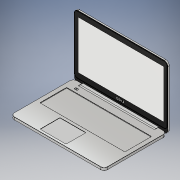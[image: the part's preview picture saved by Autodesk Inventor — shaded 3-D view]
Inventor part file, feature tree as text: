
AUTODESK INVENTOR PART (.ipt)
format: ipt  version: 2018 (Build 220112000, 112)  size: 2,366,464 bytes
history: native  units: in
note: dims shown in document units (in); Inventor stores cm internally (conversion verified against a paired STEP export)
features: imported_body x119, split x4, sketch x4, boolean_combine x3, projected_geometry x1
ambient origin geometry x8: Origin, YZ Plane, XZ Plane, XY Plane, X Axis, Y Axis, Z Axis, Center Point
bodies: Solid1 (feature_tree), Solid2 (feature_tree), Solid3 (feature_tree), Solid4 (feature_tree), Solid5 (feature_tree), Solid6 (feature_tree), Solid7 (feature_tree), Solid8 (feature_tree), Solid9 (feature_tree), Solid10 (feature_tree), Solid11 (feature_tree), Solid12 (feature_tree), Solid13 (feature_tree), Solid14 (feature_tree), Solid15 (feature_tree), Solid16 (feature_tree), Solid17 (feature_tree), Solid18 (feature_tree), Solid19 (feature_tree), Solid20 (feature_tree), Solid21 (feature_tree), Solid22 (feature_tree), Solid23 (feature_tree), Solid24 (feature_tree), Solid25 (feature_tree), Solid26 (feature_tree), Solid27 (feature_tree), Solid28 (feature_tree), Solid29 (feature_tree), Solid30 (feature_tree), Solid31 (feature_tree), Solid32 (feature_tree), Solid33 (feature_tree), Solid34 (feature_tree), Solid35 (feature_tree), Solid36 (feature_tree), Solid37 (feature_tree), Solid38 (feature_tree), Solid39 (feature_tree), Solid40 (feature_tree), Solid41 (feature_tree), Solid42 (feature_tree), Solid43 (feature_tree), Solid44 (feature_tree), Solid45 (feature_tree), Solid46 (feature_tree), Solid47 (feature_tree), Solid48 (feature_tree), Solid49 (feature_tree), Solid50 (feature_tree), Solid51 (feature_tree), Solid52 (feature_tree), Solid53 (feature_tree), Solid54 (feature_tree), Solid55 (feature_tree), Solid56 (feature_tree), Solid57 (feature_tree), Solid58 (feature_tree), Solid59 (feature_tree), Solid60 (feature_tree), Solid61 (feature_tree), Solid62 (feature_tree), Solid63 (feature_tree), Solid64 (feature_tree), Solid65 (feature_tree), Solid66 (feature_tree), Solid67 (feature_tree), Solid68 (feature_tree), Solid69 (feature_tree), Solid70 (feature_tree), Solid71 (feature_tree), Solid72 (feature_tree), Solid73 (feature_tree), Solid74 (feature_tree), Solid75 (feature_tree), Solid76 (feature_tree), Solid77 (feature_tree), Solid78 (feature_tree), Solid79 (feature_tree), Solid80 (feature_tree), Solid81 (feature_tree), Solid82 (feature_tree), Solid83 (feature_tree), Solid84 (feature_tree), Solid85 (feature_tree), Solid86 (feature_tree), Solid87 (feature_tree), Solid88 (feature_tree), Solid89 (feature_tree), Solid90 (feature_tree), Solid91 (feature_tree), Solid92 (feature_tree), Solid93 (feature_tree), Solid94 (feature_tree), Solid95 (feature_tree), Solid96 (feature_tree), Solid97 (feature_tree), Solid98 (feature_tree), Solid99 (feature_tree), Solid100 (feature_tree), Solid101 (feature_tree), Solid102 (feature_tree), Solid103 (feature_tree), Solid104 (feature_tree), Solid105 (feature_tree), Solid106 (feature_tree), Solid107 (feature_tree), Solid108 (feature_tree), Solid109 (feature_tree), Solid110 (feature_tree), Solid111 (feature_tree), Solid112 (feature_tree), Solid113 (feature_tree), Solid114 (feature_tree), Solid115 (feature_tree), Solid116 (feature_tree), Solid117 (feature_tree), Solid118 (feature_tree), Solid119 (feature_tree)
feature tree (131):
  imported_body  "Base2"
  imported_body  "Base3"
  imported_body  "Base4"
  imported_body  "Base5"
  imported_body  "Base7"
  split  "Split1"
  split  "Split2"
  split  "Split3"
  split  "Split4"
  boolean_combine  "Combine1"
  boolean_combine  "Combine2"
  boolean_combine  "Combine3"
  sketch  "Sketch1"
  projected_geometry  "Projected Loop1"
  sketch  "Sketch2"
  sketch  "Sketch3"
  sketch  "Sketch4"
  imported_body  "Base1"
  imported_body  "Base6"
  imported_body  "Base8"
  imported_body  "Base9"
  imported_body  "Base10"
  imported_body  "Base11"
  imported_body  "Base12"
  imported_body  "Base13"
  imported_body  "Base14"
  imported_body  "Base15"
  imported_body  "Base16"
  imported_body  "Base17"
  imported_body  "Base18"
  imported_body  "Base19"
  imported_body  "Base20"
  imported_body  "Base21"
  imported_body  "Base22"
  imported_body  "Base23"
  imported_body  "Base24"
  imported_body  "Base25"
  imported_body  "Base26"
  imported_body  "Base27"
  imported_body  "Base28"
  imported_body  "Base29"
  imported_body  "Base30"
  imported_body  "Base31"
  imported_body  "Base32"
  imported_body  "Base33"
  imported_body  "Base34"
  imported_body  "Base35"
  imported_body  "Base36"
  imported_body  "Base37"
  imported_body  "Base38"
  imported_body  "Base39"
  imported_body  "Base40"
  imported_body  "Base41"
  imported_body  "Base42"
  imported_body  "Base43"
  imported_body  "Base44"
  imported_body  "Base45"
  imported_body  "Base46"
  imported_body  "Base47"
  imported_body  "Base48"
  imported_body  "Base49"
  imported_body  "Base50"
  imported_body  "Base51"
  imported_body  "Base52"
  imported_body  "Base53"
  imported_body  "Base54"
  imported_body  "Base55"
  imported_body  "Base56"
  imported_body  "Base57"
  imported_body  "Base58"
  imported_body  "Base59"
  imported_body  "Base60"
  imported_body  "Base61"
  imported_body  "Base62"
  imported_body  "Base63"
  imported_body  "Base64"
  imported_body  "Base65"
  imported_body  "Base66"
  imported_body  "Base67"
  imported_body  "Base68"
  imported_body  "Base69"
  imported_body  "Base70"
  imported_body  "Base71"
  imported_body  "Base72"
  imported_body  "Base73"
  imported_body  "Base74"
  imported_body  "Base75"
  imported_body  "Base76"
  imported_body  "Base77"
  imported_body  "Base78"
  imported_body  "Base79"
  imported_body  "Base80"
  imported_body  "Base81"
  imported_body  "Base82"
  imported_body  "Base83"
  imported_body  "Base84"
  imported_body  "Base85"
  imported_body  "Base86"
  imported_body  "Base87"
  imported_body  "Base88"
  imported_body  "Base89"
  imported_body  "Base90"
  imported_body  "Base91"
  imported_body  "Base92"
  imported_body  "Base93"
  imported_body  "Base94"
  imported_body  "Base95"
  imported_body  "Base96"
  imported_body  "Base97"
  imported_body  "Base98"
  imported_body  "Base99"
  imported_body  "Base100"
  imported_body  "Base101"
  imported_body  "Base102"
  imported_body  "Base103"
  imported_body  "Base104"
  imported_body  "Base105"
  imported_body  "Base106"
  imported_body  "Base107"
  imported_body  "Base108"
  imported_body  "Base109"
  imported_body  "Base110"
  imported_body  "Base111"
  imported_body  "Base112"
  imported_body  "Base113"
  imported_body  "Base114"
  imported_body  "Base115"
  imported_body  "Base116"
  imported_body  "Base117"
  imported_body  "Base118"
  imported_body  "Base119"
